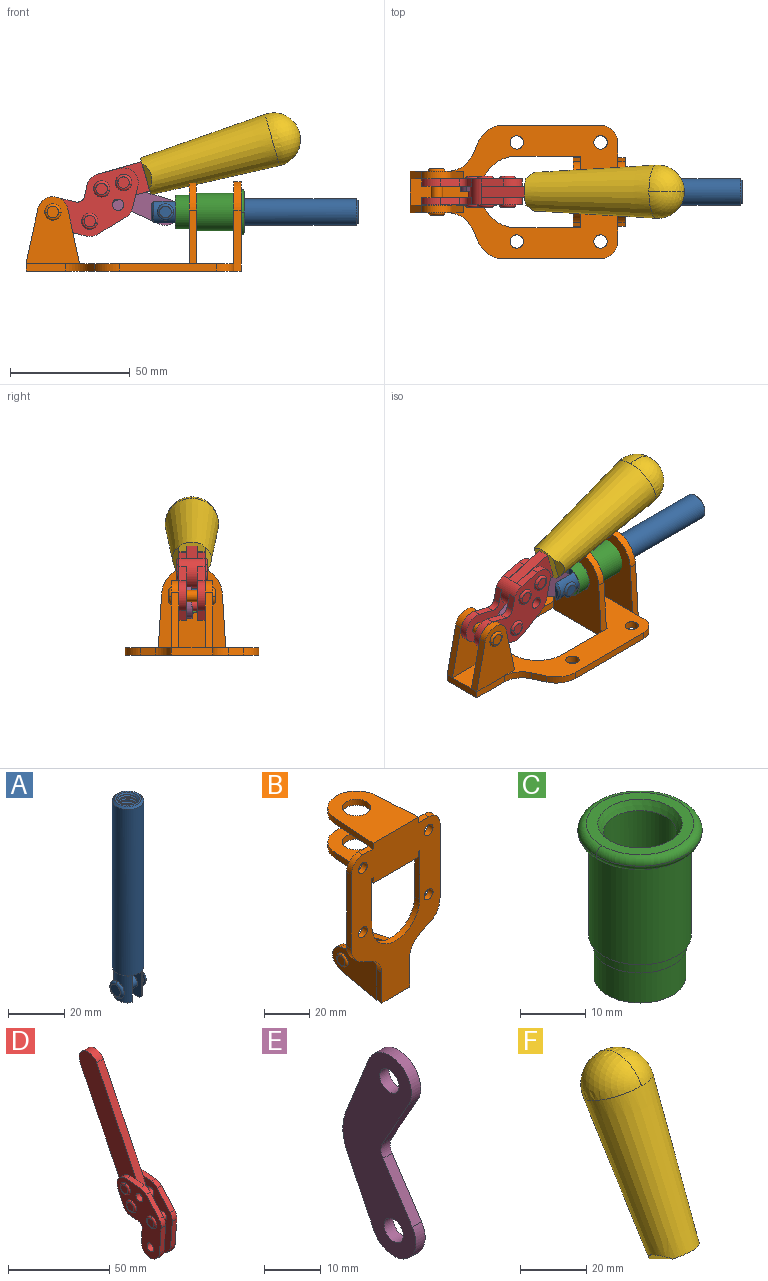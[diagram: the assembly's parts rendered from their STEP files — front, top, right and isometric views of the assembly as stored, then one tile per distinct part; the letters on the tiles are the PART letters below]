
ASSEMBLY  parts=6 mates=6
PART A: 48 faces, bbox 12.6x11.1x86.1 mm
  f0: torus R=2.41mm, axis (-1,0,0), area 15mm2, adj f30,f32,f34
  f1: torus R=2.41mm, axis (-1,0,0), area 15mm2, adj f29,f31,f33
  f2: cylinder r=5.54mm len=72.39mm, axis (0,0,1), area 2518.5mm2, adj f3,f4,f42,f43
  f3: cone r=5.54mm half-angle=45deg, axis (0,0,1), area 7.6mm2, adj f2,f5,f41
  f4: cone r=5.54mm half-angle=45deg, axis (0,0,-1), area 34.9mm2, adj f2,f39
  f5: cylinder r=5.08mm len=11.48mm, axis (0,0,1), area 108.3mm2, adj f3,f7,f8,f41
  f6: cylinder r=2.41mm len=4.83mm, axis (-1,0,0), area 71.2mm2, adj f40,f41
  f7: cylinder r=2.41mm len=4.83mm, axis (-1,0,0), area 7.6mm2, adj f5,f34
  f8: cone r=5.08mm half-angle=45deg, axis (0,0,1), area 10.6mm2, adj f5,f37,f41
  f9: cone r=3.98mm half-angle=45deg, axis (0,0,1), area 17.6mm2, adj f27,f39,f45,f46,f47
  f10: cylinder r=2.41mm len=4.83mm, axis (-1,0,0), area 7.6mm2, adj f33,f38
  f11: cylinder r=3.2mm len=6.4mm, axis (0,0,1), area 78.4mm2, adj f12,f28,f44,f45,f47
  f12: cylinder r=3.2mm len=6.4mm, axis (0,0,1), area 10.5mm2, adj f11,f13,f45,f47
  f13: cylinder r=3.2mm len=6.4mm, axis (0,0,1), area 10.5mm2, adj f12,f14,f45,f47
  f14: cylinder r=3.2mm len=6.4mm, axis (0,0,1), area 10.5mm2, adj f13,f15,f45,f47
  f15: cylinder r=3.2mm len=6.4mm, axis (0,0,1), area 10.5mm2, adj f14,f16,f45,f47
  f16: cylinder r=3.2mm len=6.4mm, axis (0,0,1), area 10.5mm2, adj f15,f17,f45,f47
  f17: cylinder r=3.2mm len=6.4mm, axis (0,0,1), area 10.5mm2, adj f16,f18,f45,f47
  f18: cylinder r=3.2mm len=6.4mm, axis (0,0,1), area 10.5mm2, adj f17,f19,f45,f47
  f19: cylinder r=3.2mm len=6.4mm, axis (0,0,1), area 10.5mm2, adj f18,f20,f45,f47
  f20: cylinder r=3.2mm len=6.4mm, axis (0,0,1), area 10.5mm2, adj f19,f21,f45,f47
  f21: cylinder r=3.2mm len=6.4mm, axis (0,0,1), area 10.5mm2, adj f20,f22,f45,f47
  f22: cylinder r=3.2mm len=6.4mm, axis (0,0,1), area 10.5mm2, adj f21,f23,f45,f47
  f23: cylinder r=3.2mm len=6.4mm, axis (0,0,1), area 10.5mm2, adj f22,f24,f45,f47
  f24: cylinder r=3.2mm len=6.4mm, axis (0,0,1), area 10.5mm2, adj f23,f25,f45,f47
  f25: cylinder r=3.2mm len=6.4mm, axis (0,0,1), area 10.5mm2, adj f24,f26,f45,f47
  f26: cylinder r=3.2mm len=6.4mm, axis (0,0,1), area 10.5mm2, adj f25,f27,f45,f47
  f27: cylinder r=3.2mm len=6.4mm, axis (0,0,1), area 7.4mm2, adj f9,f26,f45,f47
  f28: cone r=3.2mm half-angle=60deg, axis (0,0,1), area 37.2mm2, adj f11
  f29: plane 4.83x4.83mm, normal (-1,0,0), area 18.3mm2, adj f1,f31
  f30: plane 4.83x4.83mm, normal (1,0,0), area 18.3mm2, adj f0,f32
  f31: torus R=2.41mm, axis (-1,0,0), area 15mm2, adj f1,f29,f33
  f32: torus R=2.41mm, axis (-1,0,0), area 15mm2, adj f0,f30,f34
  f33: plane 6.83x6.83mm, normal (1,0,0), area 18.3mm2, adj f1,f10,f31
  f34: plane 6.83x6.83mm, normal (-1,0,0), area 18.3mm2, adj f0,f7,f32
  f35: cone r=5.08mm half-angle=45deg, axis (0,0,1), area 10.6mm2, adj f36,f38,f40
  f36: plane 7.25x1.97mm, normal (0,0,-1), area 10mm2, adj f35,f40
  f37: plane 7.25x1.97mm, normal (0,0,-1), area 10mm2, adj f8,f41
  f38: cylinder r=5.08mm len=11.48mm, axis (0,0,1), area 108.3mm2, adj f10,f35,f40,f42
  f39: plane 9.55x9.55mm, normal (0,0,1), area 22mm2, adj f4,f9
  f40: plane 12.76x10.09mm, normal (1,0,0), area 95.7mm2, adj f6,f35,f36,f38,f42,f43
  f41: plane 12.76x10.09mm, normal (-1,0,0), area 95.7mm2, adj f3,f5,f6,f8,f37,f43
  f42: cone r=5.54mm half-angle=45deg, axis (0,0,1), area 7.6mm2, adj f2,f38,f40
  f43: plane 11.07x4.7mm, normal (0,0,-1), area 50.4mm2, adj f2,f40,f41
  f44: plane 0.89x0.62mm, normal (-1,0,0), area 0.3mm2, adj f11,f45,f46,f47
  f45: bspline ~24.8x7.63mm, area 266.6mm2, adj f9,f11,f12,f13,f14,f15,f16,f17
  f46: bspline ~24.87x7.63mm, area 73.6mm2, adj f9,f44,f45,f47
  f47: bspline ~24.98x7.63mm, area 272.5mm2, adj f9,f11,f12,f13,f14,f15,f16,f17
PART B: 55 faces, bbox 55.7x37.4x89.8 mm
  f0: torus R=2.41mm, axis (-1,0,0), area 15mm2, adj f11,f15,f25
  f1: torus R=2.41mm, axis (-1,0,0), area 15mm2, adj f10,f12,f22
  f2: cylinder r=2.78mm len=5.56mm, axis (0,-1,0), area 54.2mm2, adj f30,f54
  f3: cylinder r=14.99mm len=29.97mm, axis (0,-1,0), area 145.9mm2, adj f30,f49,f53,f54
  f4: cylinder r=2.78mm len=5.56mm, axis (0,-1,0), area 54.2mm2, adj f30,f54
  f5: cylinder r=2.78mm len=5.56mm, axis (0,-1,0), area 54.2mm2, adj f30,f54
  f6: cylinder r=2.78mm len=5.56mm, axis (0,-1,0), area 54.2mm2, adj f30,f54
  f7: cylinder r=6.35mm len=12.7mm, axis (0,0,1), area 123.6mm2, adj f27,f51
  f8: cylinder r=6.35mm len=12.7mm, axis (0,0,-1), area 124.7mm2, adj f21,f35
  f9: cylinder r=2.41mm len=11.18mm, axis (-1,0,0), area 169.4mm2, adj f16,f19
  f10: plane 4.83x4.83mm, normal (1,0,0), area 18.3mm2, adj f1,f12
  f11: plane 4.83x4.83mm, normal (-1,0,0), area 18.3mm2, adj f0,f15
  f12: torus R=2.41mm, axis (-1,0,0), area 15mm2, adj f1,f10,f22
  f13: cylinder r=6.35mm len=12.41mm, axis (1,0,0), area 53.4mm2, adj f18,f19,f22,f23
  f14: cylinder r=6.35mm len=12.41mm, axis (-1,0,0), area 53.4mm2, adj f16,f17,f24,f25
  f15: torus R=2.41mm, axis (-1,0,0), area 15mm2, adj f0,f11,f25
  f16: plane 27.86x22.35mm, normal (1,0,0), area 425.4mm2, adj f9,f14,f17,f24,f30
  f17: plane 22.86x4.97mm, normal (0,0.21,0.98), area 72.5mm2, adj f14,f16,f25,f30
  f18: plane 22.86x4.97mm, normal (0,0.21,0.98), area 72.5mm2, adj f13,f19,f22,f30
  f19: plane 27.86x22.35mm, normal (-1,0,0), area 425.4mm2, adj f9,f13,f18,f23,f30
  f20: cylinder r=12.7mm len=25.35mm, axis (0,0,-1), area 119.8mm2, adj f21,f34,f35,f36
  f21: plane 34.21x28.07mm, normal (0,0,-1), area 702.4mm2, adj f8,f20,f30,f34,f36
  f22: plane 27.96x22.45mm, normal (1,0,0), area 407.2mm2, adj f1,f12,f13,f18,f23,f30,f42,f43
  f23: plane 22.86x4.97mm, normal (0,0.21,-0.98), area 72.5mm2, adj f13,f19,f22,f44
  f24: plane 22.86x4.97mm, normal (0,0.21,-0.98), area 72.5mm2, adj f14,f16,f25,f44
  f25: plane 27.86x22.35mm, normal (-1,0,0), area 407.1mm2, adj f0,f14,f15,f17,f24,f30,f45,f46
  f26: plane 3.1x0.95mm, normal (0,0,-1), area 2.7mm2, adj f30,f49,f50,f54
  f27: plane 34.21x28.07mm, normal (0,0,1), area 702.4mm2, adj f7,f28,f30,f50,f52
  f28: cylinder r=12.7mm len=25.35mm, axis (0,0,1), area 118.8mm2, adj f27,f50,f51,f52
  f29: plane 3.1x0.95mm, normal (0,0,-1), area 2.7mm2, adj f30,f52,f53,f54
  f30: plane 86.54x55.63mm, normal (0,1,0), area 2362.9mm2, adj f2,f3,f4,f5,f6,f16,f17,f18
  f31: plane 40.56x3.1mm, normal (-1,0,0), area 125.7mm2, adj f30,f32,f48,f54
  f32: cylinder r=7.11mm len=7.11mm, axis (0,-1,0), area 34.6mm2, adj f30,f31,f33,f54
  f33: plane 6.67x3.1mm, normal (0,0,1), area 20.4mm2, adj f30,f32,f34,f54
  f34: plane 25.39x3.13mm, normal (-1,0.06,0), area 79.5mm2, adj f20,f21,f33,f35,f54
  f35: plane 37.31x28.45mm, normal (0,0,1), area 789.9mm2, adj f8,f20,f34,f36,f54
  f36: plane 25.39x3.13mm, normal (1,0.06,0), area 79.5mm2, adj f20,f21,f35,f37,f54
  f37: plane 6.67x3.1mm, normal (0,0,1), area 20.4mm2, adj f30,f36,f38,f54
  f38: cylinder r=7.11mm len=7.11mm, axis (0,-1,0), area 34.6mm2, adj f30,f37,f39,f54
  f39: plane 40.56x3.1mm, normal (1,0,0), area 125.7mm2, adj f30,f38,f40,f54
  f40: cylinder r=11.18mm len=10.16mm, axis (0,-1,0), area 39.5mm2, adj f30,f39,f41,f54
  f41: plane 6.09x3.1mm, normal (0.42,0,-0.91), area 20.8mm2, adj f30,f40,f42,f54
  f42: cylinder r=11.18mm len=9.41mm, axis (0,-1,0), area 37.2mm2, adj f22,f30,f41,f43,f54
  f43: plane 16.5x3.1mm, normal (1,0,0), area 51.1mm2, adj f22,f42,f44,f54
  f44: plane 17.37x3.1mm, normal (0,0,-1), area 53.8mm2, adj f23,f24,f30,f43,f45,f54
  f45: plane 16.5x3.1mm, normal (-1,0,0), area 51.1mm2, adj f25,f44,f46,f54
  f46: cylinder r=11.18mm len=9.41mm, axis (0,-1,0), area 37.2mm2, adj f25,f30,f45,f47,f54
  f47: plane 6.09x3.1mm, normal (-0.42,0,-0.91), area 20.8mm2, adj f30,f46,f48,f54
  f48: cylinder r=11.18mm len=10.16mm, axis (0,-1,0), area 39.5mm2, adj f30,f31,f47,f54
  f49: plane 26.54x3.1mm, normal (-1,0,0), area 82.3mm2, adj f3,f26,f30,f54
  f50: plane 25.39x3.1mm, normal (1,0.06,0), area 78.8mm2, adj f26,f27,f28,f51,f54
  f51: plane 37.31x28.45mm, normal (0,0,-1), area 789.9mm2, adj f7,f28,f50,f52,f54
  f52: plane 25.39x3.1mm, normal (-1,0.06,0), area 78.8mm2, adj f27,f28,f29,f51,f54
  f53: plane 26.54x3.1mm, normal (1,0,0), area 82.3mm2, adj f3,f29,f30,f54
  f54: plane 89.66x55.63mm, normal (0,-1,0), area 2678.5mm2, adj f2,f3,f4,f5,f6,f26,f29,f31
PART C: 15 faces, bbox 20.6x20.6x28.7 mm
  f0: torus R=8.26mm, axis (0,0,1), area 56.8mm2, adj f1,f10,f12
  f1: torus R=8.26mm, axis (0,0,1), area 56.8mm2, adj f0,f6,f13
  f2: cylinder r=5.59mm len=25.91mm, axis (0,0,1), area 909.6mm2, adj f3,f4
  f3: cone r=6.86mm half-angle=45deg, axis (0,0,-1), area 70.2mm2, adj f2,f14
  f4: cone r=6.47mm half-angle=30deg, axis (0,0,1), area 66.7mm2, adj f2,f13
  f5: cylinder r=7.04mm len=14.07mm, axis (0,0,1), area 252.6mm2, adj f11,f14
  f6: torus R=8.26mm, axis (0,0,1), area 56.8mm2, adj f1,f12,f13
  f7: cylinder r=7.16mm len=14.33mm, axis (0,0,1), area 91.5mm2, adj f9,f11
  f8: cylinder r=7.86mm len=18.42mm, axis (0,0,1), area 909.6mm2, adj f9,f10
  f9: plane 15.72x15.72mm, normal (0,0,-1), area 33mm2, adj f7,f8
  f10: plane 16.51x16.51mm, normal (0,0,-1), area 19.9mm2, adj f0,f8,f12
  f11: plane 14.33x14.33mm, normal (0,0,-1), area 5.7mm2, adj f5,f7
  f12: torus R=8.26mm, axis (0,0,1), area 56.8mm2, adj f0,f6,f10
  f13: plane 16.51x16.51mm, normal (0,0,1), area 82.7mm2, adj f1,f4,f6
  f14: plane 14.07x14.07mm, normal (0,0,-1), area 7.8mm2, adj f3,f5
PART D: 59 faces, bbox 12.9x60.2x99.6 mm
  f0: torus R=2.39mm, axis (-1,0,0), area 14.9mm2, adj f20,f43,f51
  f1: torus R=2.39mm, axis (-1,0,0), area 14.9mm2, adj f19,f42,f51
  f2: torus R=2.39mm, axis (-1,0,0), area 14.9mm2, adj f18,f35,f51
  f3: torus R=2.39mm, axis (-1,0,0), area 14.9mm2, adj f14,f17,f23
  f4: torus R=2.39mm, axis (-1,0,0), area 14.9mm2, adj f13,f16,f23
  f5: torus R=2.39mm, axis (-1,0,0), area 14.9mm2, adj f12,f15,f23
  f6: cylinder r=2.39mm len=4.78mm, axis (1,0,0), area 46.5mm2, adj f48,f50,f51
  f7: cylinder r=2.39mm len=4.78mm, axis (1,0,0), area 46.5mm2, adj f50,f51
  f8: cylinder r=6.35mm len=12.68mm, axis (1,0,0), area 61.8mm2, adj f38,f39,f50,f51
  f9: cylinder r=2.39mm len=4.78mm, axis (-1,0,0), area 70.5mm2, adj f46,f50
  f10: cylinder r=2.39mm len=4.78mm, axis (-1,0,0), area 46.5mm2, adj f23,f45,f46
  f11: cylinder r=2.39mm len=4.78mm, axis (-1,0,0), area 46.5mm2, adj f23,f46
  f12: plane 4.78x4.78mm, normal (1,0,0), area 17.9mm2, adj f5,f15
  f13: plane 4.78x4.78mm, normal (1,0,0), area 17.9mm2, adj f4,f16
  f14: plane 4.78x4.78mm, normal (1,0,0), area 17.9mm2, adj f3,f17
  f15: torus R=2.39mm, axis (-1,0,0), area 14.9mm2, adj f5,f12,f23
  f16: torus R=2.39mm, axis (-1,0,0), area 14.9mm2, adj f4,f13,f23
  f17: torus R=2.39mm, axis (-1,0,0), area 14.9mm2, adj f3,f14,f23
  f18: plane 4.78x4.78mm, normal (-1,0,0), area 17.9mm2, adj f2,f35
  f19: plane 4.78x4.78mm, normal (-1,0,0), area 17.9mm2, adj f1,f42
  f20: plane 4.78x4.78mm, normal (-1,0,0), area 17.9mm2, adj f0,f43
  f21: plane 2.26x0.2mm, normal (1,0,0), area 0.2mm2, adj f31,f44
  f22: plane 2.26x0.2mm, normal (-1,0,0), area 0.2mm2, adj f41,f44
  f23: plane 39.37x30.77mm, normal (1,0,0), area 565.5mm2, adj f3,f4,f5,f10,f11,f15,f16,f17
  f24: cylinder r=6.1mm len=4.15mm, axis (-1,0,0), area 14.7mm2, adj f23,f25,f32,f46
  f25: plane 10.25x9.01mm, normal (0,-0.75,0.66), area 42.3mm2, adj f23,f24,f26,f46
  f26: cylinder r=6.35mm len=4.64mm, axis (-1,0,0), area 15.6mm2, adj f23,f25,f27,f46
  f27: plane 15.84x3.1mm, normal (0,-1,-0.07), area 49.2mm2, adj f23,f26,f28,f46
  f28: cylinder r=6.35mm len=12.68mm, axis (-1,0,0), area 61.8mm2, adj f23,f27,f29,f46
  f29: plane 8.11x3.1mm, normal (0,1,0.07), area 25.2mm2, adj f23,f28,f30,f46
  f30: cylinder r=3.05mm len=3.25mm, axis (-1,0,0), area 14.8mm2, adj f23,f29,f31,f46
  f31: plane 5.99x3.1mm, normal (0,0.07,-1), area 18.6mm2, adj f21,f23,f30,f44,f46
  f32: plane 9.5x3.1mm, normal (0,-0.07,1), area 29.5mm2, adj f23,f24,f33,f46,f47
  f33: cylinder r=6.1mm len=8.63mm, axis (-1,0,0), area 39.1mm2, adj f23,f32,f34,f47
  f34: plane 8.65x3.96mm, normal (0,0.91,-0.42), area 29.5mm2, adj f23,f33,f44,f47
  f35: torus R=2.39mm, axis (-1,0,0), area 14.9mm2, adj f2,f18,f51
  f36: plane 10.25x9.01mm, normal (0,-0.75,0.66), area 42.3mm2, adj f37,f49,f50,f51
  f37: cylinder r=6.35mm len=4.64mm, axis (1,0,0), area 15.6mm2, adj f36,f38,f50,f51
  f38: plane 15.84x3.1mm, normal (0,-1,-0.07), area 49.2mm2, adj f8,f37,f50,f51
  f39: plane 8.11x3.1mm, normal (0,1,0.07), area 25.2mm2, adj f8,f40,f50,f51
  f40: cylinder r=3.05mm len=3.25mm, axis (1,0,0), area 14.8mm2, adj f39,f41,f50,f51
  f41: plane 5.99x3.1mm, normal (0,0.07,-1), area 18.6mm2, adj f22,f40,f44,f50,f51
  f42: torus R=2.39mm, axis (-1,0,0), area 14.9mm2, adj f1,f19,f51
  f43: torus R=2.39mm, axis (-1,0,0), area 14.9mm2, adj f0,f20,f51
  f44: cylinder r=6.35mm len=12.12mm, axis (-1,0,0), area 128.9mm2, adj f21,f22,f23,f31,f34,f41,f46,f47
  f45: plane 2.65x1.35mm, normal (1,0,0), area 1mm2, adj f10,f55
  f46: plane 39.08x20.42mm, normal (-1,0,0), area 412.5mm2, adj f9,f10,f11,f24,f25,f26,f27,f28
  f47: plane 77.62x39.82mm, normal (1,0,0), area 850mm2, adj f32,f33,f34,f44,f53,f54,f55
  f48: plane 2.65x1.35mm, normal (-1,0,0), area 1mm2, adj f6,f55
  f49: cylinder r=6.1mm len=4.15mm, axis (1,0,0), area 14.7mm2, adj f36,f50,f51,f56
  f50: plane 39.08x20.42mm, normal (1,0,0), area 412.5mm2, adj f6,f7,f8,f9,f36,f37,f38,f39
  f51: plane 39.37x30.77mm, normal (-1,0,0), area 565.5mm2, adj f0,f1,f2,f6,f7,f8,f35,f36
  f52: plane 8.65x3.96mm, normal (0,0.91,-0.42), area 29.5mm2, adj f44,f51,f57,f58
  f53: plane 68.49x33.4mm, normal (0,0.9,-0.44), area 358.1mm2, adj f44,f47,f54,f58
  f54: cylinder r=6.35mm len=12.06mm, axis (1,0,0), area 93.7mm2, adj f47,f53,f55,f58
  f55: plane 68.49x33.4mm, normal (0,-0.9,0.44), area 358.1mm2, adj f44,f45,f46,f47,f48,f50,f54,f58
  f56: plane 9.5x3.1mm, normal (0,-0.07,1), area 29.5mm2, adj f49,f50,f51,f57,f58
  f57: cylinder r=6.1mm len=8.63mm, axis (1,0,0), area 39.1mm2, adj f51,f52,f56,f58
  f58: plane 77.62x39.82mm, normal (-1,0,0), area 850mm2, adj f44,f52,f53,f54,f55,f56,f57
PART E: 12 faces, bbox 2.3x18.2x42.8 mm
  f0: cylinder r=2.4mm len=4.8mm, axis (1,0,0), area 34.9mm2, adj f4,f11
  f1: cylinder r=10.41mm len=8.47mm, axis (1,0,0), area 20.2mm2, adj f4,f9,f10,f11
  f2: cylinder r=3.05mm len=3.16mm, axis (1,0,0), area 7.7mm2, adj f4,f6,f7,f11
  f3: cylinder r=2.4mm len=4.8mm, axis (1,0,0), area 34.9mm2, adj f4,f11
  f4: plane 42.81x18.23mm, normal (-1,0,0), area 414.1mm2, adj f0,f1,f2,f3,f5,f6,f7,f8
  f5: cylinder r=5.54mm len=10.67mm, axis (1,0,0), area 41.8mm2, adj f4,f6,f10,f11
  f6: plane 11.66x6.53mm, normal (0,-0.87,-0.49), area 30.9mm2, adj f2,f4,f5,f11
  f7: plane 11.17x7.33mm, normal (0,-0.84,0.55), area 30.9mm2, adj f2,f4,f8,f11
  f8: cylinder r=5.54mm len=10.51mm, axis (1,0,0), area 41.8mm2, adj f4,f7,f9,f11
  f9: plane 13.67x6.67mm, normal (0,0.9,-0.44), area 35.1mm2, adj f1,f4,f8,f11
  f10: plane 14.1x5.7mm, normal (0,0.93,0.37), area 35.1mm2, adj f1,f4,f5,f11
  f11: plane 42.81x18.23mm, normal (1,0,0), area 414.1mm2, adj f0,f1,f2,f3,f5,f6,f7,f8
PART F: 11 faces, bbox 22.3x42.6x64.5 mm
  f0: sphere r=11.13mm, area 411.4mm2, adj f1,f8
  f1: cone r=11.11mm half-angle=3.3deg, axis (0,0.44,0.9), area 3251.8mm2, adj f0,f7,f8,f9,f10
  f2: cylinder r=6.16mm len=11.7mm, axis (1,0,0), area 89.5mm2, adj f3,f4,f5,f6
  f3: plane 60.23x36.75mm, normal (-1,0,0), area 763.6mm2, adj f2,f4,f6,f10
  f4: plane 51.37x25.05mm, normal (0,0.9,-0.44), area 264.2mm2, adj f2,f3,f5,f10
  f5: plane 60.23x36.75mm, normal (1,0,0), area 763.6mm2, adj f2,f4,f6,f10
  f6: plane 51.37x25.05mm, normal (0,-0.9,0.44), area 264.2mm2, adj f2,f3,f5,f10
  f7: plane 9.95x5.95mm, normal (0.71,-0.31,-0.64), area 25.8mm2, adj f1,f10
  f8: sphere r=11.13mm, area 411.4mm2, adj f0,f1
  f9: plane 9.95x5.95mm, normal (-0.71,-0.31,-0.64), area 25.8mm2, adj f1,f10
  f10: plane 14.27x11.38mm, normal (0,-0.44,-0.9), area 106.7mm2, adj f1,f3,f4,f5,f6,f7,f9
PLACE A rot(axis=(0.58,0.58,0.58),120deg) t=(-2.21,0,-18.66)mm
PLACE B rot(axis=(0.58,0.58,0.58),120deg) t=(-1.56,0,-18.66)mm fixed
PLACE C rot(axis=(-0.58,0.58,-0.58),120deg) t=(-2.83,0,30.57)mm
PLACE D rot(axis=(0.61,0.61,0.51),125.9deg) t=(-6.32,0,-23.86)mm
PLACE E rot(axis=(0.56,0.56,0.61),117.2deg) t=(-0.03,1.16,-19.9)mm
PLACE F rot(axis=(0.61,0.61,0.51),125.9deg) t=(-6.32,0.04,-23.86)mm
MATE revolute E.f0 <-> A.f6  axis (0,-1,0) through (13.27,0,5.96)mm
MATE revolute D.f7 <-> B.f0  axis (0,-1,0) through (-33.65,0,5.96)mm
MATE fastened F.f2 <-> D.f54  axis (0,-1,0) through (59.95,2.35,36.59)mm
MATE slider A.f2 <-> C.f2  axis (1,0,0) through (56.57,0,5.96)mm
MATE revolute E.f3 <-> D.f4  axis (0,-1,0) through (-18.25,0,2.12)mm
MATE fastened C.f2 <-> B.f7  axis (1,0,0) through (44.83,0,5.96)mm
